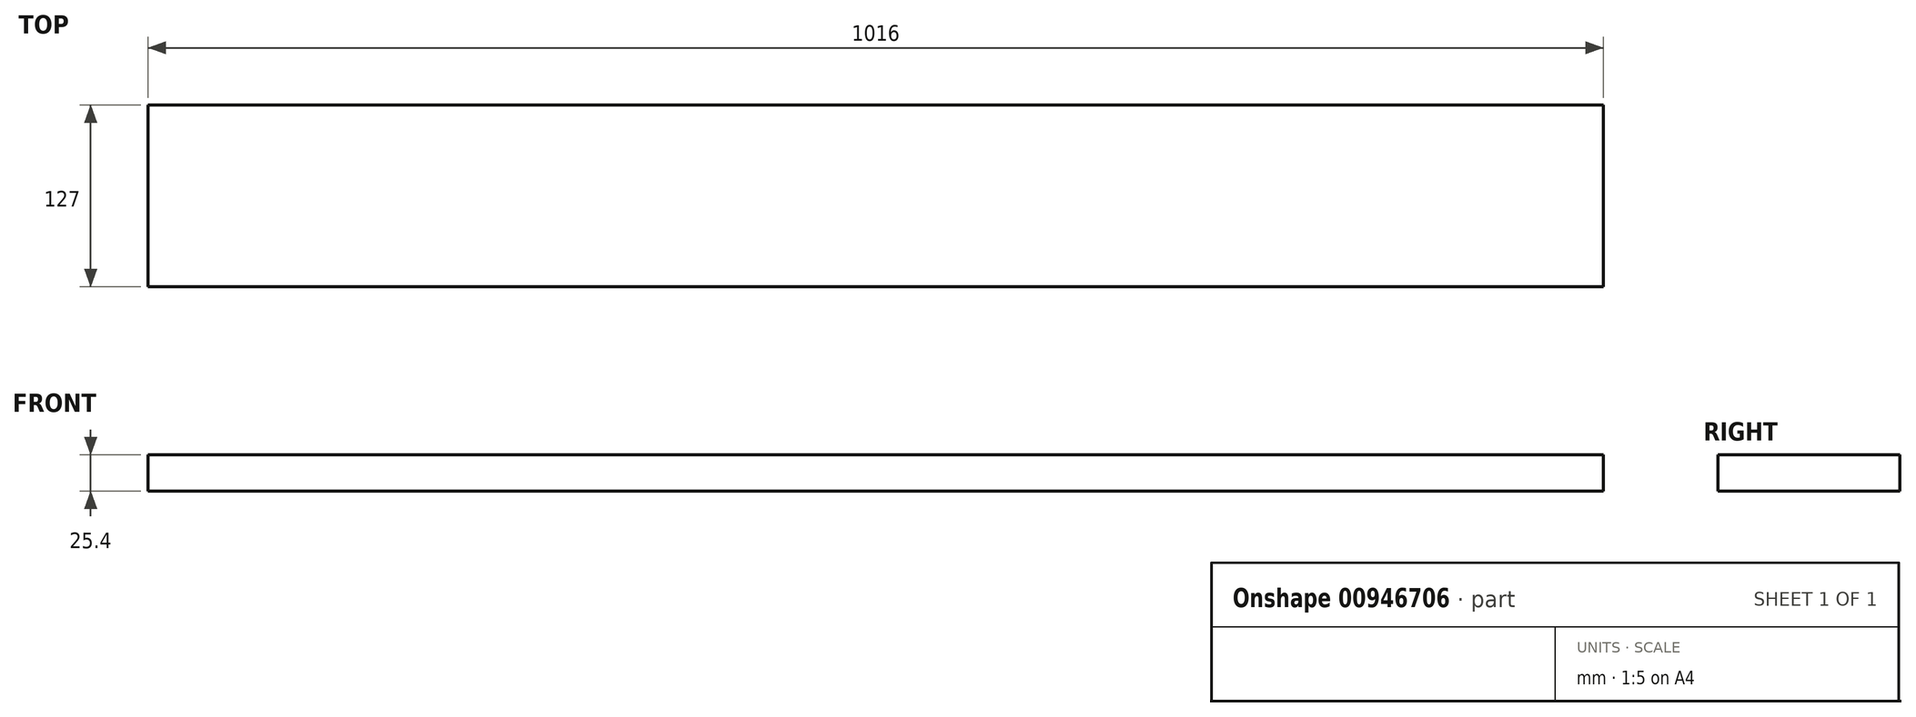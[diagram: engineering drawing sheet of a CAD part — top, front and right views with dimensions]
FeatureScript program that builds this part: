
annotation { "Feature Type Name" : "Feature", "Feature Type Description" : "" }
export const myFeature = defineFeature(function(context is Context, id is Id, definition is map)
    precondition{}
    {
        {
            var Q0;
            Q0=qCreatedBy(makeId("Top.planeOp"),FACE);
            var sketch = newSketch(context, id + "F0", { "sketchPlane" : qUnion([Q0])});
            skLineSegment(sketch, "E0.bottom", {"start": v(508, 63.5) * mm, "end": v(-508, 63.5) * mm});
            skLineSegment(sketch, "E0.top", {"start": v(508, -63.5) * mm, "end": v(-508, -63.5) * mm});
            skLineSegment(sketch, "E0.left", {"start": v(508, 63.5) * mm, "end": v(508, -63.5) * mm});
            skLineSegment(sketch, "E0.right", {"start": v(-508, 63.5) * mm, "end": v(-508, -63.5) * mm});
            skPoint(sketch, "E0.middle", {"position": v(0, 0) * mm});
            skSolve(sketch);
        }
        {
            var Q0;
            Q0 = qSketchRegion(id + "F0", true);
            extrude(context, id + "F1", {"entities" : qUnion([Q0]), "depth" : 25.4 * mm, "offsetDistance" : 25.4 * mm});
        }
    });
